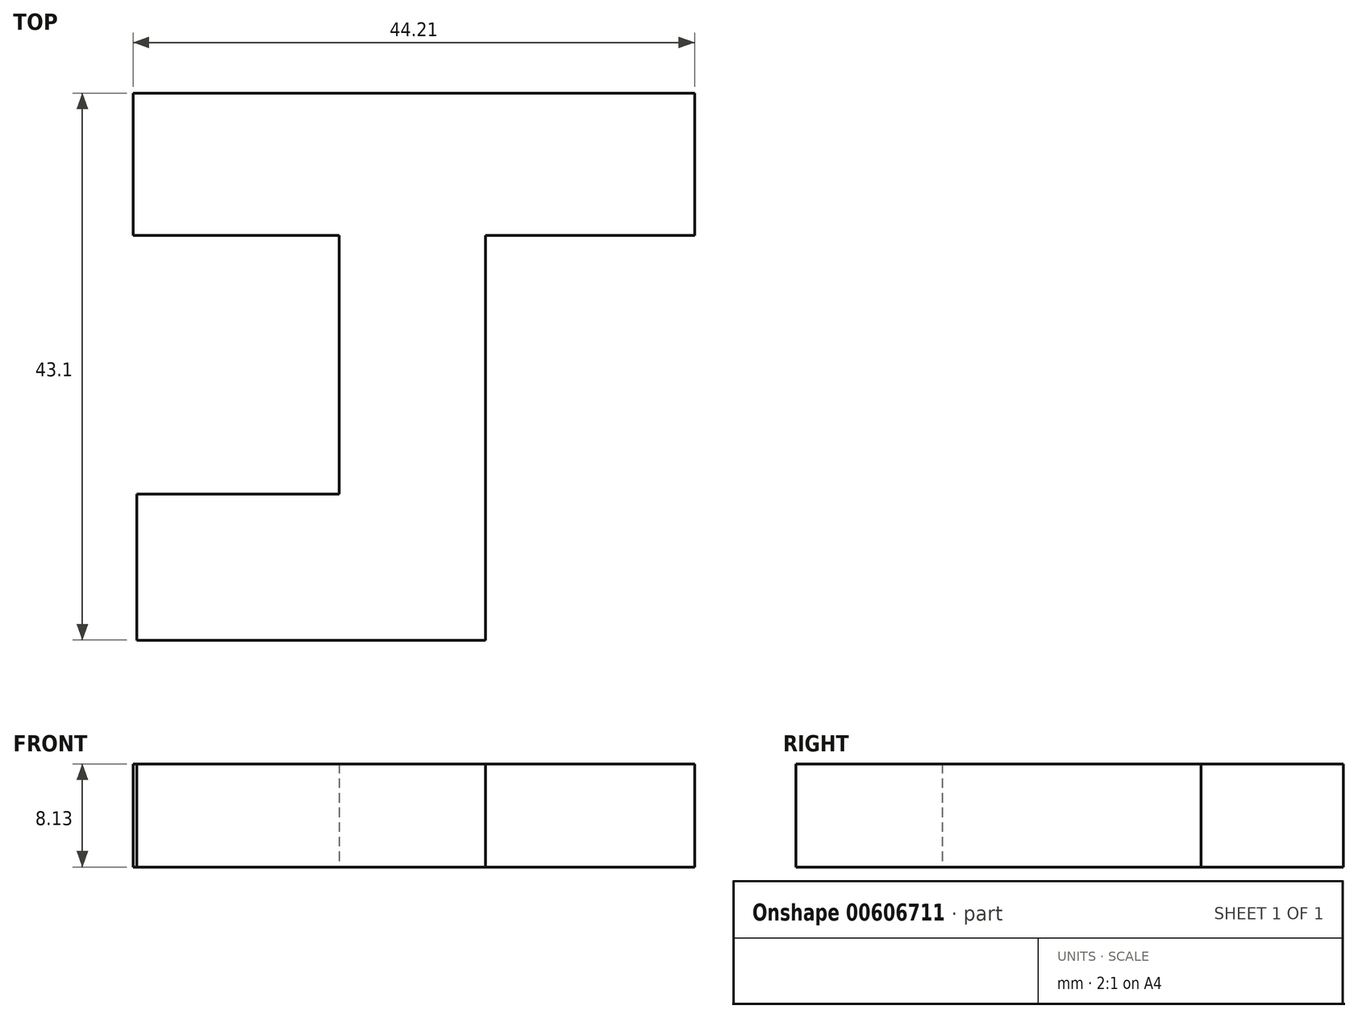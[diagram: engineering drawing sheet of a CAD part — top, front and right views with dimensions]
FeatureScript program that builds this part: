
annotation { "Feature Type Name" : "Feature", "Feature Type Description" : "" }
export const myFeature = defineFeature(function(context is Context, id is Id, definition is map)
    precondition{}
    {
        {
            var Q0;
            Q0=qCreatedBy(makeId("Top.planeOp"),FACE);
            var sketch = newSketch(context, id + "F0", { "sketchPlane" : qUnion([Q0])});
            skLineSegment(sketch, "E0.bottom", {"start": v(-44.21, 23.7) * mm, "end": v(0, 23.7) * mm});
            skLineSegment(sketch, "E0.top", {"start": v(-44.21, 12.47) * mm, "end": v(0, 12.47) * mm});
            skLineSegment(sketch, "E0.left", {"start": v(-44.21, 23.7) * mm, "end": v(-44.21, 12.47) * mm});
            skLineSegment(sketch, "E0.right", {"start": v(0, 23.7) * mm, "end": v(0, 12.47) * mm});
            skLineSegment(sketch, "E1.bottom", {"start": v(-27.97, 23.7) * mm, "end": v(-16.46, 23.7) * mm});
            skLineSegment(sketch, "E1.top", {"start": v(-27.97, -19.41) * mm, "end": v(-16.46, -19.41) * mm});
            skLineSegment(sketch, "E1.left", {"start": v(-27.97, 23.7) * mm, "end": v(-27.97, -19.41) * mm});
            skLineSegment(sketch, "E1.right", {"start": v(-16.46, 23.7) * mm, "end": v(-16.46, -19.41) * mm});
            skLineSegment(sketch, "E2.bottom", {"start": v(-16.46, -19.41) * mm, "end": v(-43.92, -19.41) * mm});
            skLineSegment(sketch, "E2.top", {"start": v(-16.46, -7.9) * mm, "end": v(-43.92, -7.9) * mm});
            skLineSegment(sketch, "E2.left", {"start": v(-16.46, -19.41) * mm, "end": v(-16.46, -7.9) * mm});
            skLineSegment(sketch, "E2.right", {"start": v(-43.92, -19.41) * mm, "end": v(-43.92, -7.9) * mm});
            skSolve(sketch);
        }
        {
            var Q0;
            Q0 = qSketchRegion(id + "F0", true);
            extrude(context, id + "F1", {"entities" : qUnion([Q0]), "depth" : 8.13 * mm, "offsetDistance" : 25.4 * mm});
        }
    });
